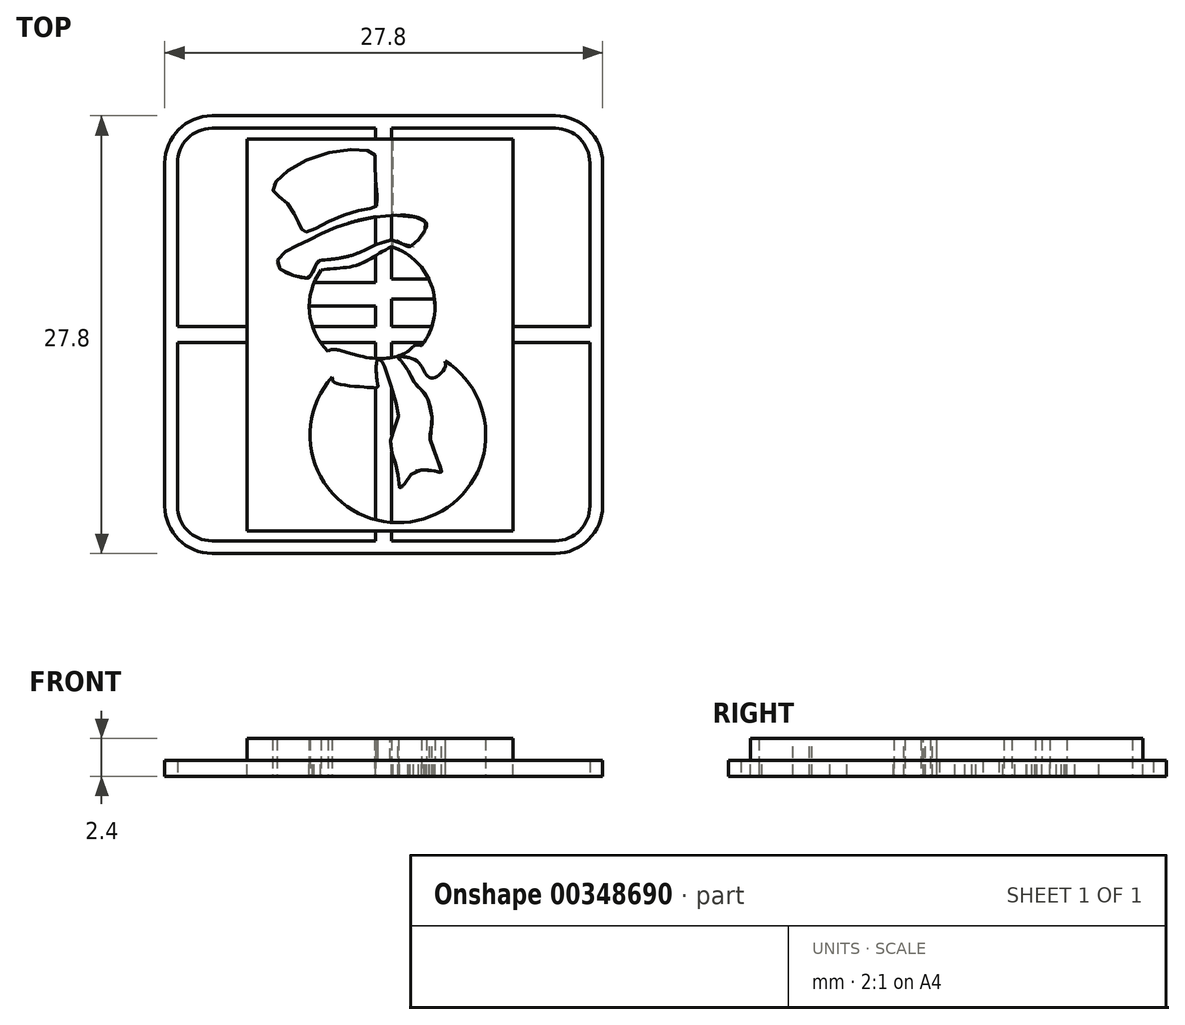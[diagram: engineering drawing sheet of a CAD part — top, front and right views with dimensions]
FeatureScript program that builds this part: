
annotation { "Feature Type Name" : "Feature", "Feature Type Description" : "" }
export const myFeature = defineFeature(function(context is Context, id is Id, definition is map)
    precondition{}
    {
        {
            var Q0;
            Q0=qCreatedBy(makeId("Top.planeOp"),FACE);
            var sketch = newSketch(context, id + "F0", { "sketchPlane" : qUnion([Q0])});
            skLineSegment(sketch, "E0", {"start": v(-13.9, 10.9) * mm, "end": v(-13.9, -10.9) * mm});
            skLineSegment(sketch, "E1", {"start": v(13.9, -10.9) * mm, "end": v(13.9, 10.9) * mm});
            skLineSegment(sketch, "E2", {"start": v(-10.9, 13.9) * mm, "end": v(10.9, 13.9) * mm});
            skLineSegment(sketch, "E3", {"start": v(-10.9, -13.9) * mm, "end": v(10.9, -13.9) * mm});
            skLineSegment(sketch, "E4", {"start": v(0, 13.9) * mm, "end": v(0, -13.9) * mm, "construction": true});
            skLineSegment(sketch, "E5", {"start": v(-13.9, 0) * mm, "end": v(13.9, 0) * mm, "construction": true});
            skPoint(sketch, "E6", {"position": v(0, 0) * mm});
            skPoint(sketch, "E7", {"position": v(0, 13.9) * mm});
            skPoint(sketch, "E8", {"position": v(0, -13.9) * mm});
            skPoint(sketch, "E9", {"position": v(-13.9, 0) * mm});
            skPoint(sketch, "E10", {"position": v(13.9, 0) * mm});
            skArc(sketch, "E11", {"start": v(-10.9, 13.9) * mm, "mid": v(-13.02, 13.02) * mm, "end": v(-13.9, 10.9) * mm});
            skArc(sketch, "E12", {"start": v(13.9, 10.9) * mm, "mid": v(13.02, 13.02) * mm, "end": v(10.9, 13.9) * mm});
            skArc(sketch, "E13", {"start": v(-13.9, -10.9) * mm, "mid": v(-13.02, -13.02) * mm, "end": v(-10.9, -13.9) * mm});
            skArc(sketch, "E14", {"start": v(10.9, -13.9) * mm, "mid": v(13.02, -13.02) * mm, "end": v(13.9, -10.9) * mm});
            skLineSegment(sketch, "E15", {"start": v(-0.5, 13.1) * mm, "end": v(-0.5, 0.5) * mm});
            skLineSegment(sketch, "E16", {"start": v(-0.5, 0.5) * mm, "end": v(-13.1, 0.5) * mm});
            skLineSegment(sketch, "E17", {"start": v(-13.1, 0.5) * mm, "end": v(-13.1, 10.9) * mm});
            skLineSegment(sketch, "E18", {"start": v(-0.5, 13.1) * mm, "end": v(-10.9, 13.1) * mm});
            skArc(sketch, "E19", {"start": v(-10.9, 13.1) * mm, "mid": v(-12.46, 12.46) * mm, "end": v(-13.1, 10.9) * mm});
            skLineSegment(sketch, "E20.MirrorCS", {"start": v(13.1, 0.5) * mm, "end": v(13.1, 10.9) * mm});
            skLineSegment(sketch, "E21.MirrorCS", {"start": v(0.5, 0.5) * mm, "end": v(13.1, 0.5) * mm});
            skLineSegment(sketch, "E22.MirrorCS", {"start": v(0.5, 13.1) * mm, "end": v(10.9, 13.1) * mm});
            skLineSegment(sketch, "E23.MirrorCS", {"start": v(0.5, 13.1) * mm, "end": v(0.5, 0.5) * mm});
            skArc(sketch, "E24.MirrorCS", {"start": v(10.9, 13.1) * mm, "mid": v(12.46, 12.46) * mm, "end": v(13.1, 10.9) * mm});
            skLineSegment(sketch, "E25.MirrorCS", {"start": v(0.5, -13.1) * mm, "end": v(10.9, -13.1) * mm});
            skLineSegment(sketch, "E26.MirrorCS", {"start": v(13.1, -0.5) * mm, "end": v(13.1, -10.9) * mm});
            skArc(sketch, "E27.MirrorCS", {"start": v(10.9, -13.1) * mm, "mid": v(12.46, -12.46) * mm, "end": v(13.1, -10.9) * mm});
            skLineSegment(sketch, "E28.MirrorCS", {"start": v(0.5, -13.1) * mm, "end": v(0.5, -0.5) * mm});
            skLineSegment(sketch, "E29.MirrorCS", {"start": v(0.5, -0.5) * mm, "end": v(13.1, -0.5) * mm});
            skLineSegment(sketch, "E30.MirrorCS", {"start": v(-0.5, -0.5) * mm, "end": v(-13.1, -0.5) * mm});
            skLineSegment(sketch, "E31.MirrorCS", {"start": v(-0.5, -13.1) * mm, "end": v(-0.5, -0.5) * mm});
            skLineSegment(sketch, "E32.MirrorCS", {"start": v(-0.5, -13.1) * mm, "end": v(-10.9, -13.1) * mm});
            skLineSegment(sketch, "E33.MirrorCS", {"start": v(-13.1, -0.5) * mm, "end": v(-13.1, -10.9) * mm});
            skArc(sketch, "E34.MirrorCS", {"start": v(-10.9, -13.1) * mm, "mid": v(-12.46, -12.46) * mm, "end": v(-13.1, -10.9) * mm});
            skLineSegment(sketch, "E35.bottom", {"start": v(-0.5, 3.3) * mm, "end": v(-6.41, 3.3) * mm});
            skLineSegment(sketch, "E35.top", {"start": v(-0.5, 1.82) * mm, "end": v(-6.41, 1.82) * mm});
            skLineSegment(sketch, "E35.left", {"start": v(-0.5, 3.3) * mm, "end": v(-0.5, 1.82) * mm});
            skLineSegment(sketch, "E35.right", {"start": v(-6.41, 3.3) * mm, "end": v(-6.41, 1.82) * mm});
            skLineSegment(sketch, "E36.bottom", {"start": v(0.5, 3.52) * mm, "end": v(4.5, 3.52) * mm});
            skLineSegment(sketch, "E36.top", {"start": v(0.5, 2.27) * mm, "end": v(4.5, 2.27) * mm});
            skLineSegment(sketch, "E36.left", {"start": v(0.5, 3.52) * mm, "end": v(0.5, 2.27) * mm});
            skLineSegment(sketch, "E36.right", {"start": v(4.5, 3.52) * mm, "end": v(4.5, 2.27) * mm});
            skSolve(sketch);
        }
        {
            var Q0;
            Q0=makeQuery(id+"F0.imprint","IMPRINT",FACE,{"disambiguationData":[TD([[makeQuery(id+"F0.imprint","IMPRINT",EDGE,{"derivedFrom":sQuery(id+"F0.wireOp",EDGE,"E0")}),1.0]])]});
            var Q1;
            {var subQ0=sQuery(id+"F0.wireOp",EDGE,"E35.bottom");Q1=makeQuery(id+"F0.imprint","IMPRINT",FACE,{"disambiguationData":[TD([[makeQuery(id+"F0.imprint","IMPRINT",EDGE,{"derivedFrom":subQ0}),1.0]])]});}
            var Q2;
            {var subQ2=sQuery(id+"F0.wireOp",EDGE,"E36.bottom");Q2=makeQuery(id+"F0.imprint","IMPRINT",FACE,{"disambiguationData":[TD([[makeQuery(id+"F0.imprint","IMPRINT",EDGE,{"derivedFrom":subQ2}),-1.0]])]});}
            extrude(context, id + "F1", {"entities" : qUnion([Q0, Q1, Q2]), "depth" : 1 * mm});
        }
        {
            var Q0;
            Q0=makeQuery(id+"F1.opExtrude","CAP_FACE",FACE,{"disambiguationData":[OSD([sQuery(id+"F0.wireOp",EDGE,"E0"),sQuery(id+"F0.wireOp",EDGE,"E1"),sQuery(id+"F0.wireOp",EDGE,"E2"),sQuery(id+"F0.wireOp",EDGE,"E3"),sQuery(id+"F0.wireOp",EDGE,"E11"),sQuery(id+"F0.wireOp",EDGE,"E12"),sQuery(id+"F0.wireOp",EDGE,"E13"),sQuery(id+"F0.wireOp",EDGE,"E14"),sQuery(id+"F0.wireOp",EDGE,"E15"),sQuery(id+"F0.wireOp",EDGE,"E16"),sQuery(id+"F0.wireOp",EDGE,"E17"),sQuery(id+"F0.wireOp",EDGE,"E18"),sQuery(id+"F0.wireOp",EDGE,"E19"),sQuery(id+"F0.wireOp",EDGE,"E20.MirrorCS"),sQuery(id+"F0.wireOp",EDGE,"E21.MirrorCS"),sQuery(id+"F0.wireOp",EDGE,"E22.MirrorCS"),sQuery(id+"F0.wireOp",EDGE,"E23.MirrorCS"),sQuery(id+"F0.wireOp",EDGE,"E24.MirrorCS"),sQuery(id+"F0.wireOp",EDGE,"E25.MirrorCS"),sQuery(id+"F0.wireOp",EDGE,"E26.MirrorCS"),sQuery(id+"F0.wireOp",EDGE,"E27.MirrorCS"),sQuery(id+"F0.wireOp",EDGE,"E28.MirrorCS"),sQuery(id+"F0.wireOp",EDGE,"E29.MirrorCS"),sQuery(id+"F0.wireOp",EDGE,"E30.MirrorCS"),sQuery(id+"F0.wireOp",EDGE,"E31.MirrorCS"),sQuery(id+"F0.wireOp",EDGE,"E32.MirrorCS"),sQuery(id+"F0.wireOp",EDGE,"E33.MirrorCS"),sQuery(id+"F0.wireOp",EDGE,"E34.MirrorCS"),sQuery(id+"F0.wireOp",EDGE,"E35.bottom"),sQuery(id+"F0.wireOp",EDGE,"E35.top"),sQuery(id+"F0.wireOp",EDGE,"E35.right"),sQuery(id+"F0.wireOp",EDGE,"E36.bottom"),sQuery(id+"F0.wireOp",EDGE,"E36.top"),sQuery(id+"F0.wireOp",EDGE,"E36.right")])],"isStart":false});
            var sketch = newSketch(context, id + "F2", { "sketchPlane" : qUnion([Q0])});
            skCircle(sketch, "E37", {"center": v(0.9, -6.38) * mm, "radius": 5.58 * mm});
            skCircle(sketch, "E38", {"center": v(-0.73, 1.78) * mm, "radius": 4 * mm});
            skFitSpline(sketch, "E39", {"points": [v(-4.6, 3.77) * mm, v(-4.9, 3.6) * mm, v(-6.7, 4.3) * mm, v(-6.4, 5.13) * mm, v(-4.97, 5.9) * mm, v(-3.05, 6.8) * mm, v(0.84, 7.6) * mm, v(2.71, 7.06) * mm, v(2.31, 6.17) * mm, v(1.6, 5.6) * mm, v(0.6, 6) * mm, v(-1.89, 5.08) * mm, v(-3.98, 4.72) * mm, v(-4.19, 4.6) * mm, v(-4.6, 3.77) * mm]});
            skFitSpline(sketch, "E40", {"points": [v(-5.2, 6.69) * mm, v(-5.5, 7.36) * mm, v(-6.4, 8.6) * mm, v(-7.04, 9.24) * mm, v(-4.72, 11.17) * mm, v(-0.66, 11.56) * mm, v(-0.57, 10.59) * mm, v(-0.43, 8.22) * mm, v(-0.87, 8) * mm, v(-3.19, 7.31) * mm, v(-4.94, 6.51) * mm, v(-5.2, 6.69) * mm]});
            skFitSpline(sketch, "E41", {"points": [v(-3.98, 4.1) * mm, v(-1.68, 4.42) * mm, v(0.5, 5.58) * mm], "startDerivative": vector(4.24, 0.81) * mm, "endDerivative": vector(4.72, 2.13) * mm});
            skFitSpline(sketch, "E42", {"points": [v(-3.53, -1.07) * mm, v(-0.93, -1.47) * mm, v(1.49, -1.1) * mm, v(1.92, -0.72) * mm, v(2.41, -0.7) * mm, v(3.9, -1.67) * mm, v(3.58, -2.51) * mm, v(2.99, -2.76) * mm, v(2.6, -2.37) * mm, v(2.1, -1.67) * mm, v(1.07, -1.4) * mm, v(0.9, -1.43) * mm, v(1.03, -1.59) * mm, v(1.48, -2.17) * mm, v(2.06, -3.19) * mm, v(2.7, -3.85) * mm, v(3.06, -5.86) * mm, v(2.94, -6.62) * mm, v(3.68, -8.72) * mm, v(3.38, -8.7) * mm, v(2.11, -8.65) * mm, v(1.48, -9.27) * mm, v(1.07, -9.8) * mm, v(0.89, -8.64) * mm, v(0.63, -7.83) * mm, v(0.44, -6.6) * mm, v(0.92, -5.32) * mm, v(0.62, -3.85) * mm, v(-0.15, -1.67) * mm, v(-0.4, -1.65) * mm, v(-0.4, -3) * mm, v(-0.4, -3.35) * mm, v(-0.66, -3.38) * mm, v(-1.1, -3.34) * mm, v(-3.07, -3.08) * mm, v(-3.28, -2.7) * mm, v(-3.53, -1.07) * mm]});
            skLineSegment(sketch, "E43.bottom", {"start": v(-8.66, 12.43) * mm, "end": v(8.23, 12.43) * mm});
            skLineSegment(sketch, "E43.top", {"start": v(-8.66, -12.5) * mm, "end": v(8.23, -12.5) * mm});
            skLineSegment(sketch, "E43.left", {"start": v(-8.66, 12.43) * mm, "end": v(-8.66, -12.5) * mm});
            skLineSegment(sketch, "E43.right", {"start": v(8.23, 12.43) * mm, "end": v(8.23, -12.5) * mm});
            skSolve(sketch);
        }
        {
            var Q0;
            Q0 = qSketchRegion(id + "F2", true);
            var Q1;
            {var subQ0=sQuery(id+"F2.wireOp",EDGE,"E38");var subQ1=sQuery(id+"F2.wireOp",EDGE,"E37");var subQ2=makeQuery(id+"F2.imprint","INTERSECT",VERTEX,{"disambiguationData":[OD(1.0)],"derivedFrom":[subQ1,subQ0]});Q1=makeQuery(id+"F2.imprint","IMPRINT",FACE,{"disambiguationData":[TD([[makeQuery(id+"F2.imprint","IMPRINT",EDGE,{"disambiguationData":[TD([[subQ2,-1.0]])],"derivedFrom":subQ1}),1.0]])]});}
            var Q2;
            {var subQ0=sQuery(id+"F2.wireOp",EDGE,"E42");var subQ1=sQuery(id+"F2.wireOp",EDGE,"E38");var subQ2=makeQuery(id+"F2.imprint","INTERSECT",VERTEX,{"disambiguationData":[OD(1.0)],"derivedFrom":[subQ1,subQ0]});Q2=makeQuery(id+"F2.imprint","IMPRINT",FACE,{"disambiguationData":[TD([[makeQuery(id+"F2.imprint","IMPRINT",EDGE,{"disambiguationData":[TD([[subQ2,1.0]])],"derivedFrom":subQ1}),-1.0]])]});}
            var Q3;
            {var subQ0=sQuery(id+"F2.wireOp",EDGE,"E38");var subQ1=sQuery(id+"F2.wireOp",EDGE,"E37");var subQ2=makeQuery(id+"F2.imprint","INTERSECT",VERTEX,{"disambiguationData":[OD(1.0)],"derivedFrom":[subQ1,subQ0]});Q3=makeQuery(id+"F2.imprint","IMPRINT",FACE,{"disambiguationData":[TD([[makeQuery(id+"F2.imprint","IMPRINT",EDGE,{"disambiguationData":[TD([[subQ2,-1.0]])],"derivedFrom":subQ1}),-1.0]])]});}
            var Q4;
            {var subQ0=sQuery(id+"F2.wireOp",EDGE,"E42");var subQ1=sQuery(id+"F2.wireOp",EDGE,"E37");var subQ2=makeQuery(id+"F2.imprint","INTERSECT",VERTEX,{"disambiguationData":[OD(2.0)],"derivedFrom":[subQ1,subQ0]});Q4=makeQuery(id+"F2.imprint","IMPRINT",FACE,{"disambiguationData":[TD([[makeQuery(id+"F2.imprint","IMPRINT",EDGE,{"disambiguationData":[TD([[subQ2,-1.0]])],"derivedFrom":subQ1}),-1.0]])]});}
            var Q5;
            {var subQ0=sQuery(id+"F2.wireOp",EDGE,"E42");var subQ1=sQuery(id+"F2.wireOp",EDGE,"E37");var subQ2=makeQuery(id+"F2.imprint","INTERSECT",VERTEX,{"disambiguationData":[OD(2.0)],"derivedFrom":[subQ1,subQ0]});Q5=makeQuery(id+"F2.imprint","IMPRINT",FACE,{"disambiguationData":[TD([[makeQuery(id+"F2.imprint","IMPRINT",EDGE,{"disambiguationData":[TD([[subQ2,-1.0]])],"derivedFrom":subQ1}),1.0]])]});}
            var Q6;
            {var subQ0=sQuery(id+"F2.wireOp",EDGE,"E38");var subQ3=sQuery(id+"F2.wireOp",EDGE,"E42");var subQ6=makeQuery(id+"F2.imprint","INTERSECT",VERTEX,{"disambiguationData":[OD(3.0)],"derivedFrom":[subQ0,subQ3]});Q6=makeQuery(id+"F2.imprint","IMPRINT",FACE,{"disambiguationData":[TD([[makeQuery(id+"F2.imprint","IMPRINT",EDGE,{"disambiguationData":[TD([[subQ6,1.0]])],"derivedFrom":subQ0}),-1.0]])]});}
            var Q7;
            {var subQ0=sQuery(id+"F2.wireOp",EDGE,"E42");var subQ1=sQuery(id+"F2.wireOp",EDGE,"E38");var subQ2=makeQuery(id+"F2.imprint","INTERSECT",VERTEX,{"disambiguationData":[OD(2.0)],"derivedFrom":[subQ1,subQ0]});Q7=makeQuery(id+"F2.imprint","IMPRINT",FACE,{"disambiguationData":[TD([[makeQuery(id+"F2.imprint","IMPRINT",EDGE,{"disambiguationData":[TD([[subQ2,-1.0]])],"derivedFrom":subQ1}),-1.0]])]});}
            var Q8;
            {var subQ0=sQuery(id+"F2.wireOp",EDGE,"E42");var subQ1=sQuery(id+"F2.wireOp",EDGE,"E38");var subQ2=makeQuery(id+"F2.imprint","INTERSECT",VERTEX,{"disambiguationData":[OD(1.0)],"derivedFrom":[subQ1,subQ0]});Q8=makeQuery(id+"F2.imprint","IMPRINT",FACE,{"disambiguationData":[TD([[makeQuery(id+"F2.imprint","IMPRINT",EDGE,{"disambiguationData":[TD([[subQ2,1.0]])],"derivedFrom":subQ1}),1.0]])]});}
            var Q9;
            {var subQ1=sQuery(id+"F2.wireOp",EDGE,"E37");var subQ5=sQuery(id+"F2.wireOp",EDGE,"E38");var subQ6=makeQuery(id+"F2.imprint","INTERSECT",VERTEX,{"disambiguationData":[OD(0.0)],"derivedFrom":[subQ1,subQ5]});Q9=makeQuery(id+"F2.imprint","IMPRINT",FACE,{"disambiguationData":[TD([[makeQuery(id+"F2.imprint","IMPRINT",EDGE,{"disambiguationData":[TD([[subQ6,-1.0]])],"derivedFrom":subQ1}),1.0]])]});}
            var Q10;
            {var subQ0=sQuery(id+"F2.wireOp",EDGE,"E38");var subQ1=sQuery(id+"F2.wireOp",EDGE,"E37");var subQ2=makeQuery(id+"F2.imprint","INTERSECT",VERTEX,{"disambiguationData":[OD(0.0)],"derivedFrom":[subQ1,subQ0]});Q10=makeQuery(id+"F2.imprint","IMPRINT",FACE,{"disambiguationData":[TD([[makeQuery(id+"F2.imprint","IMPRINT",EDGE,{"disambiguationData":[TD([[subQ2,1.0]])],"derivedFrom":subQ1}),1.0]])]});}
            var Q11;
            {var subQ0=sQuery(id+"F2.wireOp",EDGE,"E38");var subQ1=sQuery(id+"F2.wireOp",EDGE,"E37");var subQ2=makeQuery(id+"F2.imprint","INTERSECT",VERTEX,{"disambiguationData":[OD(0.0)],"derivedFrom":[subQ1,subQ0]});Q11=makeQuery(id+"F2.imprint","IMPRINT",FACE,{"disambiguationData":[TD([[makeQuery(id+"F2.imprint","IMPRINT",EDGE,{"disambiguationData":[TD([[subQ2,1.0]])],"derivedFrom":subQ1}),-1.0]])]});}
            var Q12;
            {var subQ0=sQuery(id+"F2.wireOp",EDGE,"E38");var subQ1=sQuery(id+"F2.wireOp",EDGE,"E37");var subQ2=makeQuery(id+"F2.imprint","INTERSECT",VERTEX,{"disambiguationData":[OD(0.0)],"derivedFrom":[subQ1,subQ0]});Q12=makeQuery(id+"F2.imprint","IMPRINT",FACE,{"disambiguationData":[TD([[makeQuery(id+"F2.imprint","IMPRINT",EDGE,{"disambiguationData":[TD([[subQ2,-1.0]])],"derivedFrom":subQ1}),-1.0]])]});}
            var Q13;
            {var subQ0=sQuery(id+"F2.wireOp",EDGE,"17bef67f-0edf-4978-8200-474e68df9484");Q13=makeQuery(id+"F2.imprint","IMPRINT",FACE,{"disambiguationData":[TD([[makeQuery(id+"F2.imprint","IMPRINT",EDGE,{"derivedFrom":subQ0}),-1.0]])]});}
            var Q14;
            {var subQ0=sQuery(id+"F2.wireOp",EDGE,"4432179d-8a7a-4f0f-93ba-e07aa8475e33");Q14=makeQuery(id+"F2.imprint","IMPRINT",FACE,{"disambiguationData":[TD([[makeQuery(id+"F2.imprint","IMPRINT",EDGE,{"derivedFrom":subQ0}),-1.0]])]});}
            var Q15;
            {var subQ0=sQuery(id+"F2.wireOp",EDGE,"9ZOU1D6t-NdEM-2HEr-KUk7-v3uGORUOmUtq");var subQ1=makeQuery(id+"F1.opExtrude","CAP_EDGE",EDGE,{"disambiguationData":[OSD([sQuery(id+"F0.wireOp",EDGE,"E30.MirrorCS")])],"isStart":false});var subQ2=makeQuery(id+"F2.imprint","INTERSECT",VERTEX,{"derivedFrom":[subQ1,subQ0]});Q15=makeQuery(id+"F2.imprint","IMPRINT",FACE,{"disambiguationData":[TD([[makeQuery(id+"F2.imprint","IMPRINT",EDGE,{"disambiguationData":[TD([[subQ2,-1.0]])],"derivedFrom":subQ0}),1.0]])]});}
            var Q16;
            {var subQ0=sQuery(id+"F2.wireOp",EDGE,"9ZOU1D6t-NdEM-2HEr-KUk7-v3uGORUOmUtq");var subQ1=makeQuery(id+"F1.opExtrude","CAP_EDGE",EDGE,{"disambiguationData":[OSD([sQuery(id+"F0.wireOp",EDGE,"E28.MirrorCS")])],"isStart":false});var subQ2=makeQuery(id+"F2.imprint","INTERSECT",VERTEX,{"derivedFrom":[subQ1,subQ0]});Q16=makeQuery(id+"F2.imprint","IMPRINT",FACE,{"disambiguationData":[TD([[makeQuery(id+"F2.imprint","IMPRINT",EDGE,{"disambiguationData":[TD([[subQ2,-1.0]])],"derivedFrom":subQ0}),1.0]])]});}
            var Q17;
            {var subQ0=sQuery(id+"F2.wireOp",EDGE,"2qUSpgGO-U7c2-BBUm-GBh7-hnp7a326849C");var subQ1=sQuery(id+"F2.wireOp",EDGE,"zzFwhfys-Fgs2-9Rbp-gOTm-oAmsodfUrc00");var subQ2=makeQuery(id+"F2.imprint","INTERSECT",VERTEX,{"derivedFrom":[subQ1,subQ0]});Q17=makeQuery(id+"F2.imprint","IMPRINT",FACE,{"disambiguationData":[TD([[makeQuery(id+"F2.imprint","IMPRINT",EDGE,{"disambiguationData":[TD([[subQ2,1.0]])],"derivedFrom":subQ1}),-1.0]])]});}
            var Q18;
            {var subQ1=sQuery(id+"F2.wireOp",EDGE,"hf3MsCFD-9n3h-9h2V-LkmU-ME8DCtEAD4zH");var subQ5=sQuery(id+"F2.wireOp",EDGE,"zzFwhfys-Fgs2-9Rbp-gOTm-oAmsodfUrc00");var subQ6=makeQuery(id+"F2.imprint","INTERSECT",VERTEX,{"derivedFrom":[subQ1,subQ5]});Q18=makeQuery(id+"F2.imprint","IMPRINT",FACE,{"disambiguationData":[TD([[makeQuery(id+"F2.imprint","IMPRINT",EDGE,{"disambiguationData":[TD([[subQ6,-1.0]])],"derivedFrom":subQ1}),1.0]])]});}
            var Q19;
            {var subQ0=sQuery(id+"F2.wireOp",EDGE,"hf3MsCFD-9n3h-9h2V-LkmU-ME8DCtEAD4zH");var subQ1=makeQuery(id+"F1.opExtrude","CAP_EDGE",EDGE,{"disambiguationData":[OSD([sQuery(id+"F0.wireOp",EDGE,"E15")])],"isStart":false});var subQ2=makeQuery(id+"F2.imprint","INTERSECT",VERTEX,{"disambiguationData":[OD(0.0)],"derivedFrom":[subQ1,subQ0]});Q19=makeQuery(id+"F2.imprint","IMPRINT",FACE,{"disambiguationData":[TD([[makeQuery(id+"F2.imprint","IMPRINT",EDGE,{"disambiguationData":[TD([[subQ2,-1.0]])],"derivedFrom":subQ0}),1.0]])]});}
            var Q20;
            Q20=makeQuery(id+"F2.imprint","IMPRINT",FACE,{"disambiguationData":[TD([[makeQuery(id+"F2.imprint","IMPRINT",EDGE,{"derivedFrom":sQuery(id+"F2.wireOp",EDGE,"79AMpLKg-rES3-U887-8zlP-ZagonDIGlKTe")}),1.0]])]});
            var Q21;
            {var subQ0=sQuery(id+"F2.wireOp",EDGE,"XEklnz9P-dfut-nOND-VsrR-jpSmGHGepqSu");var subQ1=makeQuery(id+"F1.opExtrude","CAP_EDGE",EDGE,{"disambiguationData":[OSD([sQuery(id+"F0.wireOp",EDGE,"E23.MirrorCS")])],"isStart":false});var subQ2=makeQuery(id+"F2.imprint","INTERSECT",VERTEX,{"disambiguationData":[OD(0.0)],"derivedFrom":[subQ1,subQ0]});Q21=makeQuery(id+"F2.imprint","IMPRINT",FACE,{"disambiguationData":[TD([[makeQuery(id+"F2.imprint","IMPRINT",EDGE,{"disambiguationData":[TD([[subQ2,-1.0]])],"derivedFrom":subQ0}),1.0]])]});}
            var Q22;
            {var subQ0=sQuery(id+"F2.wireOp",EDGE,"XEklnz9P-dfut-nOND-VsrR-jpSmGHGepqSu");var subQ1=makeQuery(id+"F1.opExtrude","CAP_EDGE",EDGE,{"disambiguationData":[OSD([sQuery(id+"F0.wireOp",EDGE,"E23.MirrorCS")])],"isStart":false});var subQ2=makeQuery(id+"F2.imprint","INTERSECT",VERTEX,{"disambiguationData":[OD(0.0)],"derivedFrom":[subQ1,subQ0]});Q22=makeQuery(id+"F2.imprint","IMPRINT",FACE,{"disambiguationData":[TD([[makeQuery(id+"F2.imprint","IMPRINT",EDGE,{"disambiguationData":[TD([[subQ2,1.0]])],"derivedFrom":subQ0}),1.0]])]});}
            var Q23;
            {var subQ0=sQuery(id+"F2.wireOp",EDGE,"E41");var subQ1=sQuery(id+"F2.wireOp",EDGE,"E38");var subQ2=makeQuery(id+"F2.imprint","INTERSECT",VERTEX,{"disambiguationData":[OD(0.0)],"derivedFrom":[subQ1,subQ0]});Q23=makeQuery(id+"F2.imprint","IMPRINT",FACE,{"disambiguationData":[TD([[makeQuery(id+"F2.imprint","IMPRINT",EDGE,{"disambiguationData":[TD([[subQ2,1.0]])],"derivedFrom":subQ1}),1.0]])]});}
            var Q24;
            {var subQ0=sQuery(id+"F2.wireOp",EDGE,"E39");var subQ5=sQuery(id+"F2.wireOp",EDGE,"E38");var subQ6=makeQuery(id+"F2.imprint","INTERSECT",VERTEX,{"disambiguationData":[OD(0.0)],"derivedFrom":[subQ5,subQ0]});Q24=makeQuery(id+"F2.imprint","IMPRINT",FACE,{"disambiguationData":[TD([[makeQuery(id+"F2.imprint","IMPRINT",EDGE,{"disambiguationData":[TD([[subQ6,1.0]])],"derivedFrom":subQ5}),1.0]])]});}
            var Q25;
            {var subQ0=sQuery(id+"F2.wireOp",EDGE,"E42");var subQ1=makeQuery(id+"F1.opExtrude","CAP_EDGE",EDGE,{"disambiguationData":[OSD([sQuery(id+"F0.wireOp",EDGE,"E28.MirrorCS")])],"isStart":false});var subQ2=makeQuery(id+"F2.imprint","INTERSECT",VERTEX,{"disambiguationData":[OD(1.0)],"derivedFrom":[subQ1,subQ0]});Q25=makeQuery(id+"F2.imprint","IMPRINT",FACE,{"disambiguationData":[TD([[makeQuery(id+"F2.imprint","IMPRINT",EDGE,{"disambiguationData":[TD([[subQ2,-1.0]])],"derivedFrom":subQ0}),-1.0]])]});}
            var Q26;
            {var subQ0=sQuery(id+"F2.wireOp",EDGE,"2qUSpgGO-U7c2-BBUm-GBh7-hnp7a326849C");var subQ1=sQuery(id+"F0.wireOp",EDGE,"E36.top");var subQ2=makeQuery(id+"F1.opExtrude","CAP_EDGE",EDGE,{"disambiguationData":[OSD([subQ1])],"isStart":false});var subQ3=makeQuery(id+"F2.imprint","INTERSECT",VERTEX,{"derivedFrom":[subQ2,subQ0]});Q26=makeQuery(id+"F2.imprint","IMPRINT",FACE,{"disambiguationData":[TD([[makeQuery(id+"F2.imprint","IMPRINT",EDGE,{"disambiguationData":[TD([[subQ3,-1.0]])],"derivedFrom":subQ0}),-1.0]])]});}
            var Q27;
            {var subQ0=sQuery(id+"F2.wireOp",EDGE,"hf3MsCFD-9n3h-9h2V-LkmU-ME8DCtEAD4zH");var subQ1=sQuery(id+"F0.wireOp",EDGE,"E35.top");var subQ2=makeQuery(id+"F1.opExtrude","CAP_EDGE",EDGE,{"disambiguationData":[OSD([subQ1])],"isStart":false});var subQ3=makeQuery(id+"F2.imprint","INTERSECT",VERTEX,{"derivedFrom":[subQ2,subQ0]});Q27=makeQuery(id+"F2.imprint","IMPRINT",FACE,{"disambiguationData":[TD([[makeQuery(id+"F2.imprint","IMPRINT",EDGE,{"disambiguationData":[TD([[subQ3,-1.0]])],"derivedFrom":subQ0}),1.0]])]});}
            extrude(context, id + "F3", {"entities" : qUnion([Q0, Q1, Q2, Q3, Q4, Q5, Q6, Q7, Q8, Q9, Q10, Q11, Q12, Q13, Q14, Q15, Q16, Q17, Q18, Q19, Q20, Q21, Q22, Q23, Q24, Q25, Q26, Q27]), "operationType" : NewBodyOperationType.ADD, "depth" : 1.4 * mm});
        }
        {
            var Q0;
            {var subQ0=sQuery(id+"F2.wireOp",EDGE,"E41");var subQ2=sQuery(id+"F2.wireOp",EDGE,"E40");var subQ7=sQuery(id+"F2.wireOp",EDGE,"E39");var subQ8=sQuery(id+"F2.wireOp",EDGE,"E42");var subQ9=sQuery(id+"F2.wireOp",EDGE,"E38");var subQ12=sQuery(id+"F0.wireOp",EDGE,"E16");var subQ16=sQuery(id+"F0.wireOp",EDGE,"E23.MirrorCS");var subQ17=sQuery(id+"F2.wireOp",EDGE,"E43.bottom");var subQ18=sQuery(id+"F2.wireOp",EDGE,"E43.left");Q0=makeQuery(id+"F3.boolean.opBoolean","SPLIT",FACE,{"disambiguationData":[TD([makeQuery(id+"F1.opExtrude","SWEPT_FACE",FACE,{"disambiguationData":[OSD([subQ12])]})])],"derivedFrom":makeQuery(id+"F3.opExtrude","CAP_FACE",FACE,{"disambiguationData":[OSD([subQ16,sQuery(id+"F2.wireOp",EDGE,"E37"),subQ9,subQ7,subQ2,subQ0,subQ8,subQ17,sQuery(id+"F2.wireOp",EDGE,"E43.top"),subQ18,sQuery(id+"F2.wireOp",EDGE,"E43.right")])],"isStart":true})});}
            var Q1;
            {var subQ0=sQuery(id+"F2.wireOp",EDGE,"E37");var subQ1=sQuery(id+"F2.wireOp",EDGE,"E43.top");var subQ3=sQuery(id+"F0.wireOp",EDGE,"E30.MirrorCS");var subQ4=sQuery(id+"F2.wireOp",EDGE,"E42");var subQ5=sQuery(id+"F2.wireOp",EDGE,"E38");var subQ14=sQuery(id+"F2.wireOp",EDGE,"E41");var subQ16=sQuery(id+"F0.wireOp",EDGE,"E23.MirrorCS");var subQ17=sQuery(id+"F2.wireOp",EDGE,"E43.left");Q1=makeQuery(id+"F3.boolean.opBoolean","SPLIT",FACE,{"disambiguationData":[TD([makeQuery(id+"F1.opExtrude","SWEPT_FACE",FACE,{"disambiguationData":[OSD([subQ3])]})])],"derivedFrom":makeQuery(id+"F3.opExtrude","CAP_FACE",FACE,{"disambiguationData":[OSD([subQ16,subQ0,subQ5,sQuery(id+"F2.wireOp",EDGE,"E39"),sQuery(id+"F2.wireOp",EDGE,"E40"),subQ14,subQ4,sQuery(id+"F2.wireOp",EDGE,"E43.bottom"),subQ1,subQ17,sQuery(id+"F2.wireOp",EDGE,"E43.right")])],"isStart":true})});}
            var Q2;
            {var subQ0=sQuery(id+"F2.wireOp",EDGE,"E37");var subQ1=sQuery(id+"F2.wireOp",EDGE,"E43.top");var subQ3=sQuery(id+"F2.wireOp",EDGE,"E38");var subQ9=sQuery(id+"F2.wireOp",EDGE,"E42");var subQ11=sQuery(id+"F2.wireOp",EDGE,"E41");var subQ13=sQuery(id+"F0.wireOp",EDGE,"E23.MirrorCS");var subQ17=sQuery(id+"F0.wireOp",EDGE,"E28.MirrorCS");var subQ18=sQuery(id+"F2.wireOp",EDGE,"E43.right");Q2=makeQuery(id+"F3.boolean.opBoolean","SPLIT",FACE,{"disambiguationData":[TD([makeQuery(id+"F1.opExtrude","SWEPT_FACE",FACE,{"disambiguationData":[OSD([subQ17])]})])],"derivedFrom":makeQuery(id+"F3.opExtrude","CAP_FACE",FACE,{"disambiguationData":[OSD([subQ13,subQ0,subQ3,sQuery(id+"F2.wireOp",EDGE,"E39"),sQuery(id+"F2.wireOp",EDGE,"E40"),subQ11,subQ9,sQuery(id+"F2.wireOp",EDGE,"E43.bottom"),subQ1,sQuery(id+"F2.wireOp",EDGE,"E43.left"),subQ18])],"isStart":true})});}
            var Q3;
            {var subQ0=sQuery(id+"F2.wireOp",EDGE,"9ZOU1D6t-NdEM-2HEr-KUk7-v3uGORUOmUtq");var subQ1=sQuery(id+"F0.wireOp",EDGE,"E21.MirrorCS");var subQ2=sQuery(id+"F2.wireOp",EDGE,"BuTKcCdE-ST6c-3t5d-foOZ-gpuw8ZRTbXGk");var subQ3=sQuery(id+"F2.wireOp",EDGE,"4432179d-8a7a-4f0f-93ba-e07aa8475e33");Q3=makeQuery(id+"F3.boolean.opBoolean","SPLIT",FACE,{"disambiguationData":[TD([makeQuery(id+"F1.opExtrude","SWEPT_FACE",FACE,{"disambiguationData":[OSD([subQ1])]})])],"derivedFrom":makeQuery(id+"F3.opExtrude","CAP_FACE",FACE,{"disambiguationData":[OSD([subQ0,subQ2,sQuery(id+"F2.wireOp",EDGE,"17bef67f-0edf-4978-8200-474e68df9484"),subQ3])],"isStart":true})});}
            var Q4;
            {var subQ0=sQuery(id+"F0.wireOp",EDGE,"E36.top");var subQ3=sQuery(id+"F2.wireOp",EDGE,"2qUSpgGO-U7c2-BBUm-GBh7-hnp7a326849C");Q4=makeQuery(id+"F3.boolean.opBoolean","SPLIT",FACE,{"disambiguationData":[TD([makeQuery(id+"F1.opExtrude","SWEPT_FACE",FACE,{"disambiguationData":[OSD([subQ0])]})])],"derivedFrom":makeQuery(id+"F3.opExtrude","CAP_FACE",FACE,{"disambiguationData":[OSD([sQuery(id+"F2.wireOp",EDGE,"hf3MsCFD-9n3h-9h2V-LkmU-ME8DCtEAD4zH"),sQuery(id+"F2.wireOp",EDGE,"zzFwhfys-Fgs2-9Rbp-gOTm-oAmsodfUrc00"),subQ3])],"isStart":true})});}
            var Q5;
            {var subQ1=sQuery(id+"F0.wireOp",EDGE,"E28.MirrorCS");var subQ2=sQuery(id+"F2.wireOp",EDGE,"9ZOU1D6t-NdEM-2HEr-KUk7-v3uGORUOmUtq");Q5=makeQuery(id+"F3.boolean.opBoolean","SPLIT",FACE,{"disambiguationData":[TD([makeQuery(id+"F1.opExtrude","SWEPT_FACE",FACE,{"disambiguationData":[OSD([subQ1])]})])],"derivedFrom":makeQuery(id+"F3.opExtrude","CAP_FACE",FACE,{"disambiguationData":[OSD([subQ2,sQuery(id+"F2.wireOp",EDGE,"BuTKcCdE-ST6c-3t5d-foOZ-gpuw8ZRTbXGk"),sQuery(id+"F2.wireOp",EDGE,"17bef67f-0edf-4978-8200-474e68df9484"),sQuery(id+"F2.wireOp",EDGE,"4432179d-8a7a-4f0f-93ba-e07aa8475e33")])],"isStart":true})});}
            var Q6;
            {var subQ1=sQuery(id+"F0.wireOp",EDGE,"E30.MirrorCS");var subQ2=sQuery(id+"F2.wireOp",EDGE,"9ZOU1D6t-NdEM-2HEr-KUk7-v3uGORUOmUtq");Q6=makeQuery(id+"F3.boolean.opBoolean","SPLIT",FACE,{"disambiguationData":[TD([makeQuery(id+"F1.opExtrude","SWEPT_FACE",FACE,{"disambiguationData":[OSD([subQ1])]})])],"derivedFrom":makeQuery(id+"F3.opExtrude","CAP_FACE",FACE,{"disambiguationData":[OSD([subQ2,sQuery(id+"F2.wireOp",EDGE,"BuTKcCdE-ST6c-3t5d-foOZ-gpuw8ZRTbXGk"),sQuery(id+"F2.wireOp",EDGE,"17bef67f-0edf-4978-8200-474e68df9484"),sQuery(id+"F2.wireOp",EDGE,"4432179d-8a7a-4f0f-93ba-e07aa8475e33")])],"isStart":true})});}
            var Q7;
            {var subQ0=sQuery(id+"F0.wireOp",EDGE,"E35.top");var subQ3=sQuery(id+"F2.wireOp",EDGE,"hf3MsCFD-9n3h-9h2V-LkmU-ME8DCtEAD4zH");Q7=makeQuery(id+"F3.boolean.opBoolean","SPLIT",FACE,{"disambiguationData":[TD([makeQuery(id+"F1.opExtrude","SWEPT_FACE",FACE,{"disambiguationData":[OSD([subQ0])]})])],"derivedFrom":makeQuery(id+"F3.opExtrude","CAP_FACE",FACE,{"disambiguationData":[OSD([subQ3,sQuery(id+"F2.wireOp",EDGE,"zzFwhfys-Fgs2-9Rbp-gOTm-oAmsodfUrc00"),sQuery(id+"F2.wireOp",EDGE,"2qUSpgGO-U7c2-BBUm-GBh7-hnp7a326849C")])],"isStart":true})});}
            var Q8;
            Q8=makeQuery(id+"F3.opExtrude","CAP_FACE",FACE,{"disambiguationData":[OSD([sQuery(id+"F2.wireOp",EDGE,"79AMpLKg-rES3-U887-8zlP-ZagonDIGlKTe")])],"isStart":true});
            var Q9;
            Q9=makeQuery(id+"F3.opExtrude","CAP_FACE",FACE,{"disambiguationData":[OSD([sQuery(id+"F2.wireOp",EDGE,"XEklnz9P-dfut-nOND-VsrR-jpSmGHGepqSu")])],"isStart":true});
            extrude(context, id + "F4", {"entities" : qUnion([Q0, Q1, Q2, Q3, Q4, Q5, Q6, Q7, Q8, Q9]), "operationType" : NewBodyOperationType.ADD, "depth" : 1 * mm});
        }
        {
            var Q0;
            {var subQ0=sQuery(id+"F2.wireOp",EDGE,"E43.bottom");var subQ2=sQuery(id+"F2.wireOp",EDGE,"E38");var subQ5=sQuery(id+"F0.wireOp",EDGE,"E21.MirrorCS");var subQ9=sQuery(id+"F2.wireOp",EDGE,"E42");var subQ10=sQuery(id+"F2.wireOp",EDGE,"E41");var subQ12=sQuery(id+"F0.wireOp",EDGE,"E23.MirrorCS");var subQ17=sQuery(id+"F2.wireOp",EDGE,"E43.right");var subQ18=sQuery(id+"F2.wireOp",EDGE,"E39");Q0=makeQuery(id+"F3.boolean.opBoolean","SPLIT",FACE,{"disambiguationData":[TD([makeQuery(id+"F1.opExtrude","SWEPT_FACE",FACE,{"disambiguationData":[OSD([subQ5])]})])],"derivedFrom":makeQuery(id+"F3.opExtrude","CAP_FACE",FACE,{"disambiguationData":[OSD([subQ12,sQuery(id+"F2.wireOp",EDGE,"E37"),subQ2,subQ18,sQuery(id+"F2.wireOp",EDGE,"E40"),subQ10,subQ9,subQ0,sQuery(id+"F2.wireOp",EDGE,"E43.top"),sQuery(id+"F2.wireOp",EDGE,"E43.left"),subQ17])],"isStart":true})});}
            var sketch = newSketch(context, id + "F5", { "sketchPlane" : qUnion([Q0])});
            skLineSegment(sketch, "E44", {"start": v(2.63, -6.52) * mm, "end": v(1.9, -5.55) * mm});
            skLineSegment(sketch, "E45", {"start": v(1.9, -5.55) * mm, "end": v(1.68, -5.6) * mm});
            skLineSegment(sketch, "E46", {"start": v(1.68, -5.6) * mm, "end": v(1.54, -5.6) * mm});
            skLineSegment(sketch, "E47", {"start": v(1.54, -5.6) * mm, "end": v(0.59, -6) * mm});
            skLineSegment(sketch, "E48", {"start": v(1, -5.39) * mm, "end": v(1.68, -5.06) * mm});
            skLineSegment(sketch, "E49", {"start": v(1.68, -5.06) * mm, "end": v(2.4, -4.28) * mm});
            skLineSegment(sketch, "E50", {"start": v(2.4, -4.28) * mm, "end": v(2.87, -3.52) * mm});
            skLineSegment(sketch, "E51", {"start": v(2.87, -3.52) * mm, "end": v(4.5, -3.52) * mm});
            skLineSegment(sketch, "E52", {"start": v(4.5, -3.52) * mm, "end": v(4.5, -2.27) * mm});
            skLineSegment(sketch, "E53", {"start": v(4.5, -2.27) * mm, "end": v(3.24, -2.27) * mm});
            skLineSegment(sketch, "E54", {"start": v(3.24, -2.27) * mm, "end": v(3.26, -1.56) * mm});
            skLineSegment(sketch, "E55", {"start": v(3.26, -1.56) * mm, "end": v(3.21, -1.12) * mm});
            skLineSegment(sketch, "E56", {"start": v(3.21, -1.12) * mm, "end": v(3.06, -0.5) * mm});
            skLineSegment(sketch, "E57", {"start": v(3.06, -0.5) * mm, "end": v(8.23, -0.5) * mm});
            skLineSegment(sketch, "E58", {"start": v(8.23, -0.5) * mm, "end": v(8.23, -12.43) * mm});
            skLineSegment(sketch, "E59", {"start": v(8.23, -12.43) * mm, "end": v(0.56, -12.43) * mm});
            skLineSegment(sketch, "E60", {"start": v(0.56, -12.43) * mm, "end": v(0.56, -7.59) * mm});
            skLineSegment(sketch, "E61", {"start": v(0.56, -7.59) * mm, "end": v(2.2, -7.42) * mm});
            skLineSegment(sketch, "E62", {"start": v(0.59, -6) * mm, "end": v(0.55, -6) * mm});
            skLineSegment(sketch, "E63", {"start": v(0.55, -6) * mm, "end": v(0.56, -5.56) * mm});
            skLineSegment(sketch, "E64", {"start": v(0.56, -5.56) * mm, "end": v(1, -5.39) * mm});
            skLineSegment(sketch, "E65", {"start": v(2.63, -6.52) * mm, "end": v(2.74, -6.94) * mm});
            skLineSegment(sketch, "E66", {"start": v(2.74, -6.94) * mm, "end": v(2.56, -7.26) * mm});
            skLineSegment(sketch, "E67", {"start": v(2.56, -7.26) * mm, "end": v(2.2, -7.42) * mm});
            skSolve(sketch);
        }
        {
            var Q0;
            Q0 = qSketchRegion(id + "F5", true);
            var Q1;
            Q1=makeQuery(id+"F5.imprint","IMPRINT",FACE,{"disambiguationData":[TD([[makeQuery(id+"F5.imprint","IMPRINT",EDGE,{"derivedFrom":sQuery(id+"F5.wireOp",EDGE,"eQpAfdwt-Ydw5-rWbL-1pED-QwFJoQP6RGcb")}),-1.0]])]});
            var Q2;
            {var subQ0=sQuery(id+"F2.wireOp",EDGE,"hf3MsCFD-9n3h-9h2V-LkmU-ME8DCtEAD4zH");var subQ2=sQuery(id+"F0.wireOp",EDGE,"E21.MirrorCS");var subQ4=sQuery(id+"F2.wireOp",EDGE,"zzFwhfys-Fgs2-9Rbp-gOTm-oAmsodfUrc00");var subQ5=sQuery(id+"F2.wireOp",EDGE,"2qUSpgGO-U7c2-BBUm-GBh7-hnp7a326849C");Q2=makeQuery(id+"F3.boolean.opBoolean","SPLIT",FACE,{"disambiguationData":[TD([makeQuery(id+"F1.opExtrude","SWEPT_FACE",FACE,{"disambiguationData":[OSD([subQ2])]})])],"derivedFrom":makeQuery(id+"F3.opExtrude","CAP_FACE",FACE,{"disambiguationData":[OSD([subQ0,subQ4,subQ5])],"isStart":true})});}
            extrude(context, id + "F6", {"entities" : qUnion([Q0, Q1, Q2]), "operationType" : NewBodyOperationType.ADD, "depth" : 1 * mm});
        }
    });
